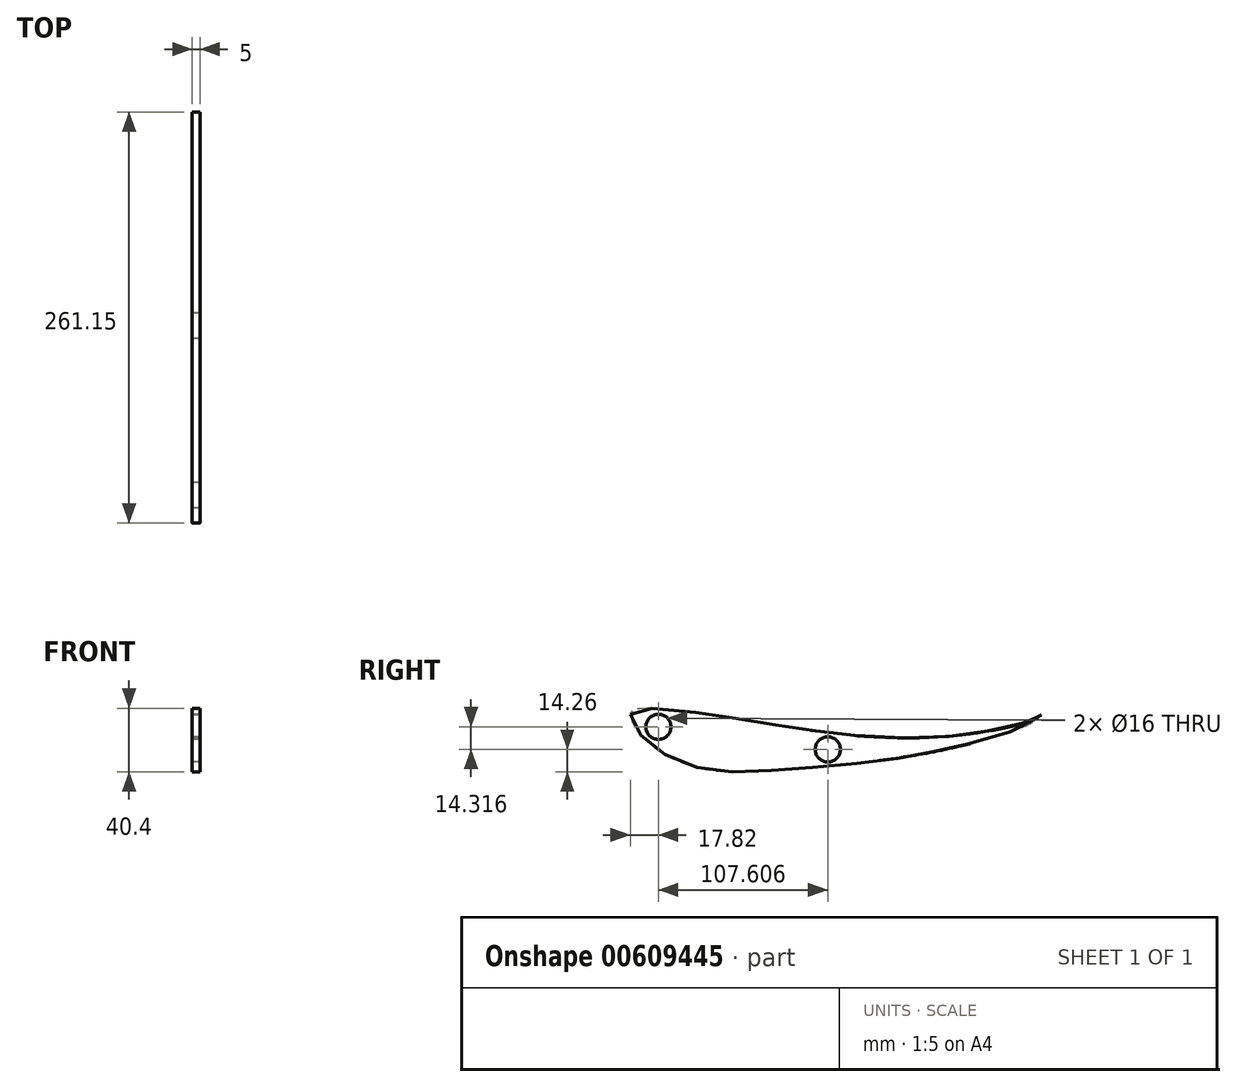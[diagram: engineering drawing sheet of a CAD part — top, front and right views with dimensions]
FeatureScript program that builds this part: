
annotation { "Feature Type Name" : "Feature", "Feature Type Description" : "" }
export const myFeature = defineFeature(function(context is Context, id is Id, definition is map)
    precondition{}
    {
        {
            var Q0;
            Q0=qCreatedBy(makeId("Right.planeOp"),FACE);
            var sketch = newSketch(context, id + "F0", { "sketchPlane" : qUnion([Q0])});
            skFitSpline(sketch, "E0", {"points": [v(-80.8, 13.24) * mm, v(-80.61, 11.37) * mm, v(-79.82, 8.81) * mm, v(-78.65, 6.38) * mm, v(-76.66, 3.33) * mm, v(-74.35, 0.36) * mm, v(-71.98, -2.03) * mm, v(-68.91, -4.81) * mm, v(-64.25, -8.53) * mm, v(-59.93, -11.46) * mm, v(-54.56, -14.38) * mm, v(-49.42, -16.84) * mm, v(-41.98, -19.4) * mm, v(-37.72, -20.63) * mm, v(-30.76, -21.93) * mm, v(-25.57, -22.58) * mm, v(-18.37, -23.12) * mm, v(-8.04, -23.12) * mm, v(-2.73, -22.9) * mm, v(4.86, -22.6) * mm, v(14.53, -21.9) * mm, v(21.53, -21.39) * mm, v(29.93, -20.72) * mm, v(41.83, -19.77) * mm, v(51.68, -18.9) * mm, v(61.29, -17.96) * mm, v(72.59, -16.71) * mm, v(79.96, -15.79) * mm, v(87.3, -14.78) * mm, v(94.64, -13.63) * mm, v(100, -12.67) * mm, v(106.52, -11.5) * mm, v(112.7, -10.33) * mm, v(118.92, -8.98) * mm, v(125.13, -7.58) * mm, v(133.8, -5.6) * mm, v(140.6, -3.74) * mm, v(150.63, -1) * mm, v(161.87, 2.7) * mm, v(168.15, 5.12) * mm, v(172.1, 7.03) * mm, v(175.67, 9.17) * mm, v(178.32, 11.3) * mm, v(180.3, 13.08) * mm, v(177.35, 11.39) * mm, v(174.34, 10.01) * mm, v(169.45, 8.14) * mm, v(164.67, 6.59) * mm, v(159.95, 5.4) * mm, v(153.63, 3.99) * mm, v(146.13, 2.64) * mm, v(138.91, 1.34) * mm, v(131.73, 0.47) * mm, v(122.4, -0.59) * mm, v(115.36, -0.99) * mm, v(105.32, -1.6) * mm, v(91.7, -1.67) * mm, v(74.3, -1.18) * mm, v(64.3, -0.42) * mm, v(58.82, 0) * mm, v(51.93, 0.77) * mm, v(44.72, 1.64) * mm, v(32.87, 3.24) * mm, v(24.44, 4.43) * mm, v(17.41, 5.66) * mm, v(8.5, 6.95) * mm, v(1.39, 8.17) * mm, v(-6.34, 9.44) * mm, v(-16.04, 11.03) * mm, v(-24.07, 12.35) * mm, v(-33.28, 13.8) * mm, v(-41.59, 14.9) * mm, v(-51.47, 15.97) * mm, v(-62.63, 16.79) * mm, v(-70.76, 17.2) * mm, v(-75.41, 16.85) * mm, v(-77.05, 16.7) * mm, v(-78.78, 16.27) * mm, v(-79.83, 15.4) * mm, v(-80.8, 13.24) * mm]});
            skPoint(sketch, "E1", {"position": v(-63.02, 5.38) * mm});
            skCircle(sketch, "E2", {"center": v(-63.02, 5.38) * mm, "radius": 8 * mm});
            skPoint(sketch, "E3", {"position": v(44.59, -8.94) * mm});
            skCircle(sketch, "E4", {"center": v(44.59, -8.94) * mm, "radius": 8 * mm});
            skSolve(sketch);
        }
        {
            var Q0;
            Q0=makeQuery(id+"F0.imprint","IMPRINT",FACE,{"disambiguationData":[TD([[makeQuery(id+"F0.imprint","IMPRINT",EDGE,{"derivedFrom":sQuery(id+"F0.wireOp",EDGE,"E0")}),1.0]])]});
            extrude(context, id + "F1", {"entities" : qUnion([Q0]), "depth" : 5 * mm, "offsetDistance" : 25.4 * mm});
        }
    });
